# Revit family: Hager-Pablo-IP55-Plain_Door-sistema-NoHosted-IT-it
name_source: partatom
category: Electrical Equipment
units: mm (PartAtom-declared; Revit-internal decimal feet)

## family parameters
Always vertical = Yes
Cut with Voids When Loaded = No
Panel Configuration = Two Columns, Circuits Across
Part Type = Panelboard
Room Calculation Point = No
Round Connector Dimension = Use Diameter
Shared = No
Work Plane-Based = Yes

## types (3) — shared parameters
Default Elevation = 1219 mm
EF000003 - Tipo di montaggio = EV000384 - A parete
EF000008 - Larghezza = 195 mm  [stored 0.639764 ft]
EF000118 - con piastra di montaggio = No
EF000266 - numero di file = 1
EF000339 - tipo di copertura = EV001012 - coperchio
EF001062 - esecuzione EMC = No
EF001088 - possibilità di applicazione = No
EF005474 - grado di protezione (IP) = EV006420 - IP55
EF006244 - coperchio/porta trasparente = No
EF009212 - esecuzione coperchio = EV009916 - con taglio
EF015777 - Morsettiera neutra = No
HG000001 - Numero di colonne = 1
HG000002 - Con porta = Yes
HG000003 - Gamma = Pablo
HG000005 - Spessore = 3 mm  [stored 0.00984252 ft]
HG000006 - Ad incasso = No
HG000009 - Porta doppia a battente = No
HG000010 - Porte asimmetriche = No
HG000011 - File vuote nella parte basse = No
HG000017 - Distanza tra i poli = 18 mm  [stored 0.0590551 ft]
Manufacturer = Hager
Type Comments = Pablo
zero-valued in all types: EF000332 - Altezza della parte incassata, EF000846 - larghezza di montaggio, HG000007 - Numero di colonne vuote, HG000008 - Numero di file vuote

## per-type parameters (varying)
| type | EF000007 - colore | EF000040 - Altezza | EF000049 - profondità | EF000116 - numero RAL | EF000218 - profondità di incasso | EF001131 - profondità interna | EF001134 - barra DIN | EF001596 - Attacco Lampada | EF002950 - Numero moduli DIN | EF004462 - tipo di chiusura | EF006306 - con serratura | EF015776 - Morsettiera di terra | EF015941 - Segnale di passaggio porta | HG000004 - Codice produttore | Model |
| A parete IP55 L195 A128 P103 4 Unità di divisione - B05762 | EV000233 - rosso | 128 mm | 103 mm | 3000 | 80 mm | 103 mm | No | EV000139 - plastica | 4 |  | Yes | No | No | B05762 | B05762 |
| A parete IP55 L195 A200 P106 8 Unità di divisione - B05764 |  | 200 mm  [stored 0.656168 ft] | 106 mm  [stored 0.347769 ft] |  | 0 mm  [stored 0 ft] | 0 mm  [stored 0 ft] | Yes |  | 8 | EV000154 - altri | No | Yes | Yes | B05764 | B05764 |
| A parete IP55 L195 A200 P106 8 Unità di divisione - B05766 |  | 200 mm  [stored 0.656168 ft] | 106 mm  [stored 0.347769 ft] |  | 0 mm  [stored 0 ft] | 0 mm  [stored 0 ft] | Yes |  | 8 | EV000154 - altri | No | Yes | Yes | B05766 | B05766 |

note: [stored X ft] marks values corroborated as IEEE doubles in the binary element streams (Revit-internal decimal feet)

## geometry (parser evidence)
native form markers: Sweep x13
no freeform markers — native parametric forms only
